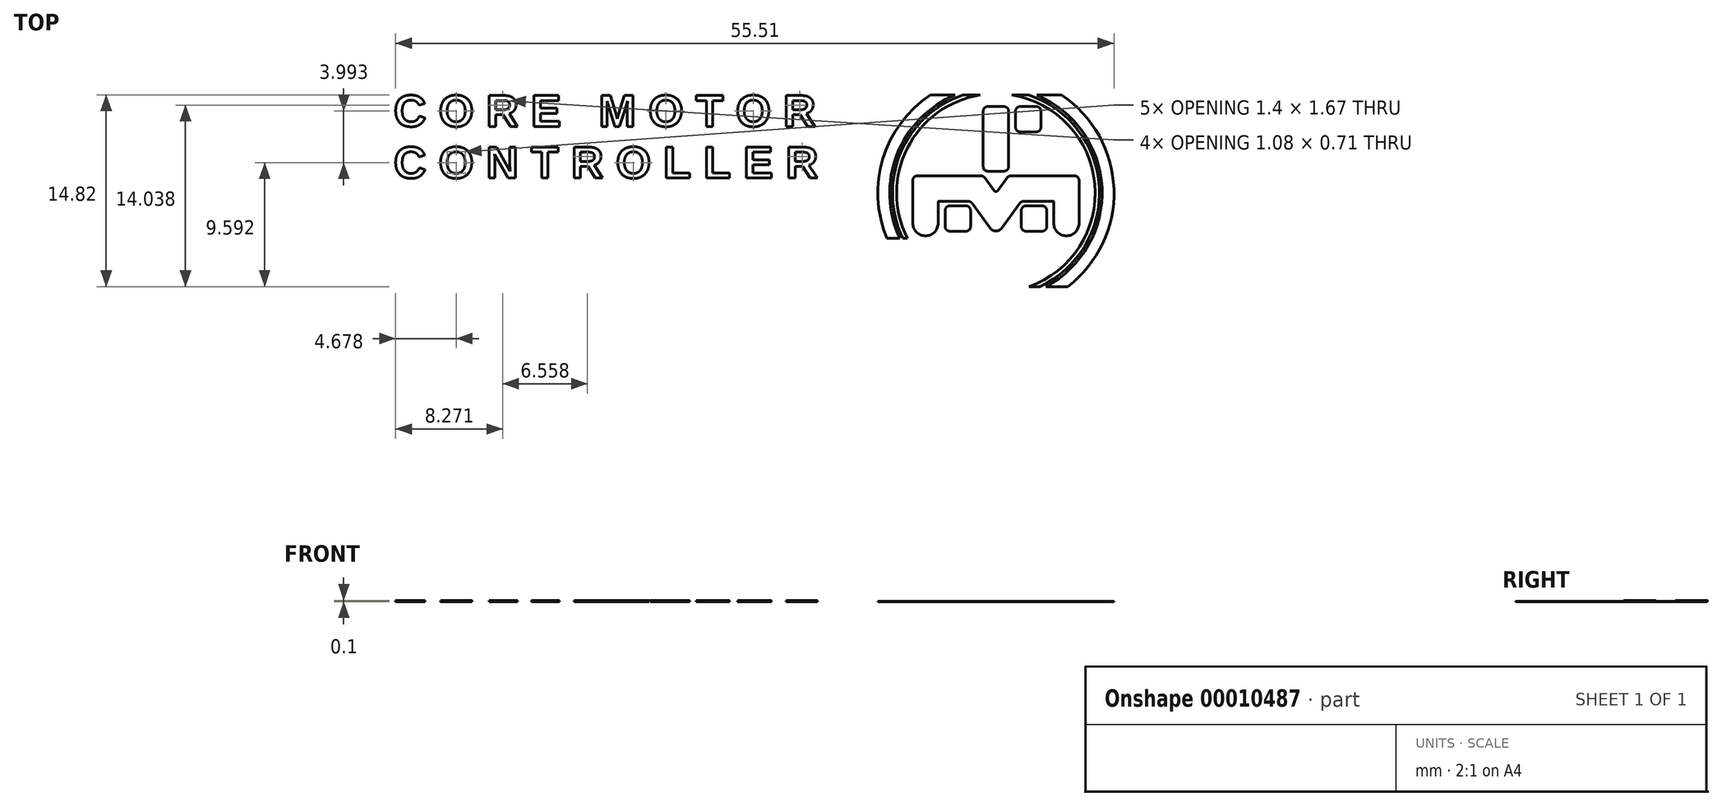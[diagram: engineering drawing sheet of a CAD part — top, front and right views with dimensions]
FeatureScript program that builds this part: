
annotation { "Feature Type Name" : "Feature", "Feature Type Description" : "" }
export const myFeature = defineFeature(function(context is Context, id is Id, definition is map)
    precondition{}
    {
        {
            var Q0;
            Q0=qCreatedBy(makeId("Top.planeOp"),FACE);
            var sketch = newSketch(context, id + "F0", { "sketchPlane" : qUnion([Q0])});
            skLineSegment(sketch, "E0.bottom", {"start": v(62.75, -5.5) * mm, "end": v(66.25, -5.5) * mm});
            skLineSegment(sketch, "E0.top", {"start": v(62.75, -19.5) * mm, "end": v(66.25, -19.5) * mm});
            skLineSegment(sketch, "E0.left", {"start": v(61.75, -6.5) * mm, "end": v(61.75, -18.5) * mm});
            skLineSegment(sketch, "E0.right", {"start": v(67.25, -6.5) * mm, "end": v(67.25, -18.5) * mm});
            skLineSegment(sketch, "E1.bottom", {"start": v(69.75, -5.5) * mm, "end": v(73.25, -5.5) * mm});
            skLineSegment(sketch, "E1.top", {"start": v(69.75, -11) * mm, "end": v(73.25, -11) * mm});
            skLineSegment(sketch, "E1.left", {"start": v(68.75, -6.5) * mm, "end": v(68.75, -10) * mm});
            skLineSegment(sketch, "E1.right", {"start": v(74.25, -6.5) * mm, "end": v(74.25, -10) * mm});
            skLineSegment(sketch, "E2", {"start": v(64.5, -19.5) * mm, "end": v(64.5, -33.5) * mm, "construction": true});
            skLineSegment(sketch, "E3", {"start": v(63.3, -31.86) * mm, "end": v(59.27, -26.4) * mm});
            skLineSegment(sketch, "E4", {"start": v(58.47, -26) * mm, "end": v(52.1, -26) * mm});
            skLineSegment(sketch, "E5", {"start": v(52, -26.1) * mm, "end": v(52, -30.75) * mm});
            skLineSegment(sketch, "E6.0", {"start": v(46.5, -21.5) * mm, "end": v(46.5, -30.75) * mm});
            skLineSegment(sketch, "E6.1", {"start": v(61.24, -20.5) * mm, "end": v(47.5, -20.5) * mm});
            skLineSegment(sketch, "E6.2", {"start": v(64.1, -23.68) * mm, "end": v(62.05, -20.9) * mm});
            skLineSegment(sketch, "E7", {"start": v(49.25, -33.5) * mm, "end": v(49.25, -33.5) * mm});
            skPoint(sketch, "E8.orphan", {"position": v(52, -33.5) * mm});
            skPoint(sketch, "E9.visualSharp", {"position": v(46.5, -33.5) * mm});
            skArc(sketch, "E9.filletArc", {"start": v(46.5, -30.75) * mm, "mid": v(47.3, -32.7) * mm, "end": v(49.25, -33.5) * mm});
            skArc(sketch, "E10.filletArc", {"start": v(49.25, -33.5) * mm, "mid": v(51.2, -32.7) * mm, "end": v(52, -30.75) * mm});
            skLineSegment(sketch, "E11.right", {"start": v(59, -28) * mm, "end": v(59, -31.5) * mm});
            skLineSegment(sketch, "E11.left", {"start": v(53.5, -28) * mm, "end": v(53.5, -31.5) * mm});
            skLineSegment(sketch, "E11.top", {"start": v(54.5, -32.5) * mm, "end": v(58, -32.5) * mm});
            skLineSegment(sketch, "E11.bottom", {"start": v(54.5, -27) * mm, "end": v(58, -27) * mm});
            skPoint(sketch, "E12.0.MirrorP", {"position": v(77, -33.5) * mm});
            skLineSegment(sketch, "E12.1.MirrorCS", {"start": v(74.5, -27) * mm, "end": v(71, -27) * mm});
            skPoint(sketch, "E12.2.MirrorP", {"position": v(82.5, -33.5) * mm});
            skLineSegment(sketch, "E12.3.MirrorCS", {"start": v(70, -28) * mm, "end": v(70, -31.5) * mm});
            skLineSegment(sketch, "E12.4.MirrorCS", {"start": v(75.5, -28) * mm, "end": v(75.5, -31.5) * mm});
            skLineSegment(sketch, "E12.5.MirrorCS", {"start": v(74.5, -32.5) * mm, "end": v(71, -32.5) * mm});
            skLineSegment(sketch, "E12.6.MirrorCS", {"start": v(70.53, -26) * mm, "end": v(76.9, -26) * mm});
            skLineSegment(sketch, "E12.7.MirrorCS", {"start": v(77, -26.1) * mm, "end": v(77, -30.75) * mm});
            skArc(sketch, "E12.8.MirrorCS", {"start": v(79.75, -33.5) * mm, "mid": v(77.8, -32.7) * mm, "end": v(77, -30.75) * mm});
            skLineSegment(sketch, "E12.9.MirrorCS", {"start": v(79.75, -33.5) * mm, "end": v(79.75, -33.5) * mm});
            skLineSegment(sketch, "E12.10.MirrorCS", {"start": v(67.76, -20.5) * mm, "end": v(81.5, -20.5) * mm});
            skPoint(sketch, "E12.11.MirrorP", {"position": v(77, -33.5) * mm});
            skLineSegment(sketch, "E12.12.MirrorCS", {"start": v(64.9, -23.68) * mm, "end": v(66.95, -20.9) * mm});
            skArc(sketch, "E12.13.MirrorCS", {"start": v(82.5, -30.75) * mm, "mid": v(81.7, -32.7) * mm, "end": v(79.75, -33.5) * mm});
            skLineSegment(sketch, "E12.14.MirrorCS", {"start": v(65.7, -31.86) * mm, "end": v(69.73, -26.4) * mm});
            skLineSegment(sketch, "E12.15.MirrorCS", {"start": v(82.5, -21.5) * mm, "end": v(82.5, -30.75) * mm});
            skPoint(sketch, "E13.visualSharp", {"position": v(68.75, -5.5) * mm});
            skArc(sketch, "E13.filletArc", {"start": v(69.75, -5.5) * mm, "mid": v(69.04, -5.8) * mm, "end": v(68.75, -6.5) * mm});
            skPoint(sketch, "E14.visualSharp", {"position": v(74.25, -5.5) * mm});
            skArc(sketch, "E14.filletArc", {"start": v(74.25, -6.5) * mm, "mid": v(73.96, -5.8) * mm, "end": v(73.25, -5.5) * mm});
            skPoint(sketch, "E15.visualSharp", {"position": v(74.25, -11) * mm});
            skArc(sketch, "E15.filletArc", {"start": v(73.25, -11) * mm, "mid": v(73.96, -10.7) * mm, "end": v(74.25, -10) * mm});
            skPoint(sketch, "E16.visualSharp", {"position": v(68.75, -11) * mm});
            skArc(sketch, "E16.filletArc", {"start": v(68.75, -10) * mm, "mid": v(69.04, -10.7) * mm, "end": v(69.75, -11) * mm});
            skPoint(sketch, "E17.visualSharp", {"position": v(67.25, -5.5) * mm});
            skArc(sketch, "E17.filletArc", {"start": v(67.25, -6.5) * mm, "mid": v(66.96, -5.8) * mm, "end": v(66.25, -5.5) * mm});
            skPoint(sketch, "E18.visualSharp", {"position": v(61.75, -5.5) * mm});
            skArc(sketch, "E18.filletArc", {"start": v(62.75, -5.5) * mm, "mid": v(62.04, -5.8) * mm, "end": v(61.75, -6.5) * mm});
            skPoint(sketch, "E19.visualSharp", {"position": v(61.75, -19.5) * mm});
            skArc(sketch, "E19.filletArc", {"start": v(61.75, -18.5) * mm, "mid": v(62.04, -19.2) * mm, "end": v(62.75, -19.5) * mm});
            skPoint(sketch, "E20.visualSharp", {"position": v(67.25, -19.5) * mm});
            skArc(sketch, "E20.filletArc", {"start": v(66.25, -19.5) * mm, "mid": v(66.96, -19.2) * mm, "end": v(67.25, -18.5) * mm});
            skPoint(sketch, "E21.visualSharp", {"position": v(70, -32.5) * mm});
            skArc(sketch, "E21.filletArc", {"start": v(70, -31.5) * mm, "mid": v(70.3, -32.2) * mm, "end": v(71, -32.5) * mm});
            skPoint(sketch, "E22.visualSharp", {"position": v(75.5, -27) * mm});
            skArc(sketch, "E22.filletArc", {"start": v(75.5, -28) * mm, "mid": v(75.2, -27.3) * mm, "end": v(74.5, -27) * mm});
            skPoint(sketch, "E23.visualSharp", {"position": v(70, -27) * mm});
            skArc(sketch, "E23.filletArc", {"start": v(71, -27) * mm, "mid": v(70.3, -27.3) * mm, "end": v(70, -28) * mm});
            skPoint(sketch, "E24.visualSharp", {"position": v(75.5, -32.5) * mm});
            skArc(sketch, "E24.filletArc", {"start": v(74.5, -32.5) * mm, "mid": v(75.2, -32.2) * mm, "end": v(75.5, -31.5) * mm});
            skPoint(sketch, "E25.visualSharp", {"position": v(59, -32.5) * mm});
            skArc(sketch, "E25.filletArc", {"start": v(58, -32.5) * mm, "mid": v(58.7, -32.2) * mm, "end": v(59, -31.5) * mm});
            skPoint(sketch, "E26.visualSharp", {"position": v(59, -27) * mm});
            skArc(sketch, "E26.filletArc", {"start": v(59, -28) * mm, "mid": v(58.7, -27.3) * mm, "end": v(58, -27) * mm});
            skPoint(sketch, "E27.visualSharp", {"position": v(53.5, -27) * mm});
            skArc(sketch, "E27.filletArc", {"start": v(54.5, -27) * mm, "mid": v(53.8, -27.3) * mm, "end": v(53.5, -28) * mm});
            skPoint(sketch, "E28.visualSharp", {"position": v(53.5, -32.5) * mm});
            skArc(sketch, "E28.filletArc", {"start": v(53.5, -31.5) * mm, "mid": v(53.8, -32.2) * mm, "end": v(54.5, -32.5) * mm});
            skPoint(sketch, "E29.visualSharp", {"position": v(46.5, -20.5) * mm});
            skArc(sketch, "E29.filletArc", {"start": v(47.5, -20.5) * mm, "mid": v(46.8, -20.8) * mm, "end": v(46.5, -21.5) * mm});
            skPoint(sketch, "E30.visualSharp", {"position": v(82.5, -20.5) * mm});
            skArc(sketch, "E30.filletArc", {"start": v(82.5, -21.5) * mm, "mid": v(82.2, -20.8) * mm, "end": v(81.5, -20.5) * mm});
            skPoint(sketch, "E31.visualSharp", {"position": v(61.75, -20.5) * mm});
            skArc(sketch, "E31.filletArc", {"start": v(62.05, -20.9) * mm, "mid": v(61.7, -20.6) * mm, "end": v(61.24, -20.5) * mm});
            skPoint(sketch, "E32.visualSharp", {"position": v(67.25, -20.5) * mm});
            skArc(sketch, "E32.filletArc", {"start": v(67.76, -20.5) * mm, "mid": v(67.3, -20.6) * mm, "end": v(66.95, -20.9) * mm});
            skPoint(sketch, "E33.visualSharp", {"position": v(52, -26) * mm});
            skArc(sketch, "E33.filletArc", {"start": v(52.1, -26) * mm, "mid": v(52.03, -26.03) * mm, "end": v(52, -26.1) * mm});
            skPoint(sketch, "E34.visualSharp", {"position": v(77, -26) * mm});
            skArc(sketch, "E34.filletArc", {"start": v(77, -26.1) * mm, "mid": v(76.97, -26.03) * mm, "end": v(76.9, -26) * mm});
            skPoint(sketch, "E35.visualSharp", {"position": v(70.03, -26) * mm});
            skArc(sketch, "E35.filletArc", {"start": v(70.53, -26) * mm, "mid": v(70.08, -26.1) * mm, "end": v(69.73, -26.4) * mm});
            skPoint(sketch, "E36.visualSharp", {"position": v(58.97, -26) * mm});
            skArc(sketch, "E36.filletArc", {"start": v(59.27, -26.4) * mm, "mid": v(58.92, -26.1) * mm, "end": v(58.47, -26) * mm});
            skPoint(sketch, "E37.visualSharp", {"position": v(64.5, -33.5) * mm});
            skArc(sketch, "E37.filletArc", {"start": v(63.3, -31.86) * mm, "mid": v(64.5, -32.47) * mm, "end": v(65.7, -31.86) * mm});
            skPoint(sketch, "E38.visualSharp", {"position": v(64.5, -24.23) * mm});
            skArc(sketch, "E38.filletArc", {"start": v(64.1, -23.68) * mm, "mid": v(64.5, -23.89) * mm, "end": v(64.9, -23.68) * mm});
            skArc(sketch, "E39", {"start": v(71.68, -44.5) * mm, "mid": v(85.92, -22.29) * mm, "end": v(67.92, -3) * mm});
            skArc(sketch, "E40", {"start": v(74, -44.5) * mm, "mid": v(86.85, -22.94) * mm, "end": v(71.6, -3) * mm});
            skArc(sketch, "E41", {"start": v(75.35, -44.5) * mm, "mid": v(87.46, -23.1) * mm, "end": v(73.32, -3) * mm});
            skArc(sketch, "E42", {"start": v(80.06, -44.5) * mm, "mid": v(90.04, -23.4) * mm, "end": v(78.72, -3) * mm});
            skLineSegment(sketch, "E43", {"start": v(80.06, -44.5) * mm, "end": v(75.35, -44.5) * mm});
            skLineSegment(sketch, "E44.trimOffspring", {"start": v(74, -44.5) * mm, "end": v(71.68, -44.5) * mm});
            skLineSegment(sketch, "E45", {"start": v(40.9, -34) * mm, "end": v(43.69, -34) * mm});
            skLineSegment(sketch, "E46.trimOffspring", {"start": v(44.36, -34) * mm, "end": v(45.34, -34) * mm});
            skLineSegment(sketch, "E47", {"start": v(50.28, -3) * mm, "end": v(55.68, -3) * mm});
            skArc(sketch, "E48.trimOffspring", {"start": v(61.08, -3) * mm, "mid": v(45.33, -14.5) * mm, "end": v(45.34, -34) * mm});
            skArc(sketch, "E49.trimOffspring", {"start": v(50.28, -3) * mm, "mid": v(40.05, -16.82) * mm, "end": v(40.9, -34) * mm});
            skArc(sketch, "E50.trimOffspring", {"start": v(55.68, -3) * mm, "mid": v(43.06, -15.94) * mm, "end": v(43.69, -34) * mm});
            skArc(sketch, "E51.trimOffspring", {"start": v(57.4, -3) * mm, "mid": v(43.86, -15.55) * mm, "end": v(44.36, -34) * mm});
            skLineSegment(sketch, "E52.trimOffspring", {"start": v(67.92, -3) * mm, "end": v(71.6, -3) * mm});
            skLineSegment(sketch, "E53.trimOffspring", {"start": v(57.4, -3) * mm, "end": v(61.08, -3) * mm});
            skLineSegment(sketch, "E54.trimOffspring", {"start": v(73.32, -3) * mm, "end": v(78.72, -3) * mm});
            skSolve(sketch);
        }
        {
            var Q0;
            Q0=makeQuery(id+"F0.imprint","IMPRINT",FACE,{"disambiguationData":[TD([[makeQuery(id+"F0.imprint","IMPRINT",EDGE,{"derivedFrom":sQuery(id+"F0.wireOp",EDGE,"46c11c21-c6ca-42b8-9659-15b4f280ee3c.sketch_text.stroke-197")}),1.0]])]});
            var Q1;
            Q1=makeQuery(id+"F0.imprint","IMPRINT",FACE,{"disambiguationData":[TD([[makeQuery(id+"F0.imprint","IMPRINT",EDGE,{"derivedFrom":sQuery(id+"F0.wireOp",EDGE,"E1.bottom")}),-1.0]])]});
            var Q2;
            Q2=makeQuery(id+"F0.imprint","IMPRINT",FACE,{"disambiguationData":[TD([[makeQuery(id+"F0.imprint","IMPRINT",EDGE,{"derivedFrom":sQuery(id+"F0.wireOp",EDGE,"46c11c21-c6ca-42b8-9659-15b4f280ee3c.sketch_text.stroke-126")}),-1.0]])]});
            var Q3;
            Q3=makeQuery(id+"F0.imprint","IMPRINT",FACE,{"disambiguationData":[TD([[makeQuery(id+"F0.imprint","IMPRINT",EDGE,{"derivedFrom":sQuery(id+"F0.wireOp",EDGE,"46c11c21-c6ca-42b8-9659-15b4f280ee3c.sketch_text.stroke-360")}),-1.0]])]});
            var Q4;
            Q4=makeQuery(id+"F0.imprint","IMPRINT",FACE,{"disambiguationData":[TD([[makeQuery(id+"F0.imprint","IMPRINT",EDGE,{"derivedFrom":sQuery(id+"F0.wireOp",EDGE,"E0.bottom")}),-1.0]])]});
            var Q5;
            Q5=makeQuery(id+"F0.imprint","IMPRINT",FACE,{"disambiguationData":[TD([[makeQuery(id+"F0.imprint","IMPRINT",EDGE,{"derivedFrom":sQuery(id+"F0.wireOp",EDGE,"46c11c21-c6ca-42b8-9659-15b4f280ee3c.sketch_text.stroke-0")}),-1.0]])]});
            var Q6;
            Q6=makeQuery(id+"F0.imprint","IMPRINT",FACE,{"disambiguationData":[TD([[makeQuery(id+"F0.imprint","IMPRINT",EDGE,{"derivedFrom":sQuery(id+"F0.wireOp",EDGE,"46c11c21-c6ca-42b8-9659-15b4f280ee3c.sketch_text.stroke-90")}),-1.0]])]});
            var Q7;
            Q7=makeQuery(id+"F0.imprint","IMPRINT",FACE,{"disambiguationData":[TD([[makeQuery(id+"F0.imprint","IMPRINT",EDGE,{"derivedFrom":sQuery(id+"F0.wireOp",EDGE,"46c11c21-c6ca-42b8-9659-15b4f280ee3c.sketch_text.stroke-145")}),-1.0]])]});
            var Q8;
            Q8=makeQuery(id+"F0.imprint","IMPRINT",FACE,{"disambiguationData":[TD([[makeQuery(id+"F0.imprint","IMPRINT",EDGE,{"derivedFrom":sQuery(id+"F0.wireOp",EDGE,"46c11c21-c6ca-42b8-9659-15b4f280ee3c.sketch_text.stroke-126")}),1.0]])]});
            var Q9;
            Q9=makeQuery(id+"F0.imprint","IMPRINT",FACE,{"disambiguationData":[TD([[makeQuery(id+"F0.imprint","IMPRINT",EDGE,{"derivedFrom":sQuery(id+"F0.wireOp",EDGE,"46c11c21-c6ca-42b8-9659-15b4f280ee3c.sketch_text.stroke-48")}),-1.0]])]});
            var Q10;
            Q10=makeQuery(id+"F0.imprint","IMPRINT",FACE,{"disambiguationData":[TD([[makeQuery(id+"F0.imprint","IMPRINT",EDGE,{"derivedFrom":sQuery(id+"F0.wireOp",EDGE,"46c11c21-c6ca-42b8-9659-15b4f280ee3c.sketch_text.stroke-239")}),1.0]])]});
            var Q11;
            Q11=makeQuery(id+"F0.imprint","IMPRINT",FACE,{"disambiguationData":[TD([[makeQuery(id+"F0.imprint","IMPRINT",EDGE,{"derivedFrom":sQuery(id+"F0.wireOp",EDGE,"E12.1.MirrorCS")}),1.0]])]});
            var Q12;
            Q12=makeQuery(id+"F0.imprint","IMPRINT",FACE,{"disambiguationData":[TD([[makeQuery(id+"F0.imprint","IMPRINT",EDGE,{"derivedFrom":sQuery(id+"F0.wireOp",EDGE,"46c11c21-c6ca-42b8-9659-15b4f280ee3c.sketch_text.stroke-300")}),-1.0]])]});
            var Q13;
            Q13=makeQuery(id+"F0.imprint","IMPRINT",FACE,{"disambiguationData":[TD([[makeQuery(id+"F0.imprint","IMPRINT",EDGE,{"derivedFrom":sQuery(id+"F0.wireOp",EDGE,"46c11c21-c6ca-42b8-9659-15b4f280ee3c.sketch_text.stroke-245")}),-1.0]])]});
            var Q14;
            Q14=makeQuery(id+"F0.imprint","IMPRINT",FACE,{"disambiguationData":[TD([[makeQuery(id+"F0.imprint","IMPRINT",EDGE,{"derivedFrom":sQuery(id+"F0.wireOp",EDGE,"46c11c21-c6ca-42b8-9659-15b4f280ee3c.sketch_text.stroke-268")}),-1.0]])]});
            var Q15;
            Q15=makeQuery(id+"F0.imprint","IMPRINT",FACE,{"disambiguationData":[TD([[makeQuery(id+"F0.imprint","IMPRINT",EDGE,{"derivedFrom":sQuery(id+"F0.wireOp",EDGE,"46c11c21-c6ca-42b8-9659-15b4f280ee3c.sketch_text.stroke-189")}),-1.0]])]});
            var Q16;
            Q16=makeQuery(id+"F0.imprint","IMPRINT",FACE,{"disambiguationData":[TD([[makeQuery(id+"F0.imprint","IMPRINT",EDGE,{"derivedFrom":sQuery(id+"F0.wireOp",EDGE,"46c11c21-c6ca-42b8-9659-15b4f280ee3c.sketch_text.stroke-114")}),-1.0]])]});
            var Q17;
            Q17=makeQuery(id+"F0.imprint","IMPRINT",FACE,{"disambiguationData":[TD([[makeQuery(id+"F0.imprint","IMPRINT",EDGE,{"derivedFrom":sQuery(id+"F0.wireOp",EDGE,"E3")}),-1.0]])]});
            var Q18;
            Q18=makeQuery(id+"F0.imprint","IMPRINT",FACE,{"disambiguationData":[TD([[makeQuery(id+"F0.imprint","IMPRINT",EDGE,{"derivedFrom":sQuery(id+"F0.wireOp",EDGE,"46c11c21-c6ca-42b8-9659-15b4f280ee3c.sketch_text.stroke-345")}),-1.0]])]});
            var Q19;
            Q19=makeQuery(id+"F0.imprint","IMPRINT",FACE,{"disambiguationData":[TD([[makeQuery(id+"F0.imprint","IMPRINT",EDGE,{"derivedFrom":sQuery(id+"F0.wireOp",EDGE,"46c11c21-c6ca-42b8-9659-15b4f280ee3c.sketch_text.stroke-232")}),1.0]])]});
            var Q20;
            Q20=makeQuery(id+"F0.imprint","IMPRINT",FACE,{"disambiguationData":[TD([[makeQuery(id+"F0.imprint","IMPRINT",EDGE,{"derivedFrom":sQuery(id+"F0.wireOp",EDGE,"46c11c21-c6ca-42b8-9659-15b4f280ee3c.sketch_text.stroke-280")}),1.0]])]});
            var Q21;
            Q21=makeQuery(id+"F0.imprint","IMPRINT",FACE,{"disambiguationData":[TD([[makeQuery(id+"F0.imprint","IMPRINT",EDGE,{"derivedFrom":sQuery(id+"F0.wireOp",EDGE,"46c11c21-c6ca-42b8-9659-15b4f280ee3c.sketch_text.stroke-161")}),-1.0]])]});
            var Q22;
            Q22=makeQuery(id+"F0.imprint","IMPRINT",FACE,{"disambiguationData":[TD([[makeQuery(id+"F0.imprint","IMPRINT",EDGE,{"derivedFrom":sQuery(id+"F0.wireOp",EDGE,"46c11c21-c6ca-42b8-9659-15b4f280ee3c.sketch_text.stroke-157")}),-1.0]])]});
            var Q23;
            Q23=makeQuery(id+"F0.imprint","IMPRINT",FACE,{"disambiguationData":[TD([[makeQuery(id+"F0.imprint","IMPRINT",EDGE,{"derivedFrom":sQuery(id+"F0.wireOp",EDGE,"46c11c21-c6ca-42b8-9659-15b4f280ee3c.sketch_text.stroke-84")}),1.0]])]});
            var Q24;
            Q24=makeQuery(id+"F0.imprint","IMPRINT",FACE,{"disambiguationData":[TD([[makeQuery(id+"F0.imprint","IMPRINT",EDGE,{"derivedFrom":sQuery(id+"F0.wireOp",EDGE,"46c11c21-c6ca-42b8-9659-15b4f280ee3c.sketch_text.stroke-60")}),-1.0]])]});
            var Q25;
            Q25=makeQuery(id+"F0.imprint","IMPRINT",FACE,{"disambiguationData":[TD([[makeQuery(id+"F0.imprint","IMPRINT",EDGE,{"derivedFrom":sQuery(id+"F0.wireOp",EDGE,"46c11c21-c6ca-42b8-9659-15b4f280ee3c.sketch_text.stroke-340")}),1.0]])]});
            var Q26;
            Q26=makeQuery(id+"F0.imprint","IMPRINT",FACE,{"disambiguationData":[TD([[makeQuery(id+"F0.imprint","IMPRINT",EDGE,{"derivedFrom":sQuery(id+"F0.wireOp",EDGE,"46c11c21-c6ca-42b8-9659-15b4f280ee3c.sketch_text.stroke-220")}),-1.0]])]});
            var Q27;
            Q27=makeQuery(id+"F0.imprint","IMPRINT",FACE,{"disambiguationData":[TD([[makeQuery(id+"F0.imprint","IMPRINT",EDGE,{"derivedFrom":sQuery(id+"F0.wireOp",EDGE,"46c11c21-c6ca-42b8-9659-15b4f280ee3c.sketch_text.stroke-76")}),-1.0]])]});
            var Q28;
            Q28=makeQuery(id+"F0.imprint","IMPRINT",FACE,{"disambiguationData":[TD([[makeQuery(id+"F0.imprint","IMPRINT",EDGE,{"derivedFrom":sQuery(id+"F0.wireOp",EDGE,"46c11c21-c6ca-42b8-9659-15b4f280ee3c.sketch_text.stroke-327")}),1.0]])]});
            var Q29;
            Q29=makeQuery(id+"F0.imprint","IMPRINT",FACE,{"disambiguationData":[TD([[makeQuery(id+"F0.imprint","IMPRINT",EDGE,{"derivedFrom":sQuery(id+"F0.wireOp",EDGE,"46c11c21-c6ca-42b8-9659-15b4f280ee3c.sketch_text.stroke-29")}),-1.0]])]});
            var Q30;
            Q30=makeQuery(id+"F0.imprint","IMPRINT",FACE,{"disambiguationData":[TD([[makeQuery(id+"F0.imprint","IMPRINT",EDGE,{"derivedFrom":sQuery(id+"F0.wireOp",EDGE,"46c11c21-c6ca-42b8-9659-15b4f280ee3c.sketch_text.stroke-60")}),1.0]])]});
            var Q31;
            Q31=makeQuery(id+"F0.imprint","IMPRINT",FACE,{"disambiguationData":[TD([[makeQuery(id+"F0.imprint","IMPRINT",EDGE,{"derivedFrom":sQuery(id+"F0.wireOp",EDGE,"46c11c21-c6ca-42b8-9659-15b4f280ee3c.sketch_text.stroke-333")}),-1.0]])]});
            var Q32;
            Q32=makeQuery(id+"F0.imprint","IMPRINT",FACE,{"disambiguationData":[TD([[makeQuery(id+"F0.imprint","IMPRINT",EDGE,{"derivedFrom":sQuery(id+"F0.wireOp",EDGE,"E11.right")}),-1.0]])]});
            var Q33;
            Q33=makeQuery(id+"F0.imprint","IMPRINT",FACE,{"disambiguationData":[TD([[makeQuery(id+"F0.imprint","IMPRINT",EDGE,{"derivedFrom":sQuery(id+"F0.wireOp",EDGE,"46c11c21-c6ca-42b8-9659-15b4f280ee3c.sketch_text.stroke-216")}),-1.0]])]});
            var Q34;
            Q34=makeQuery(id+"F0.imprint","IMPRINT",FACE,{"disambiguationData":[TD([[makeQuery(id+"F0.imprint","IMPRINT",EDGE,{"derivedFrom":sQuery(id+"F0.wireOp",EDGE,"46c11c21-c6ca-42b8-9659-15b4f280ee3c.sketch_text.stroke-260")}),-1.0]])]});
            var Q35;
            Q35=makeQuery(id+"F0.imprint","IMPRINT",FACE,{"disambiguationData":[TD([[makeQuery(id+"F0.imprint","IMPRINT",EDGE,{"derivedFrom":sQuery(id+"F0.wireOp",EDGE,"46c11c21-c6ca-42b8-9659-15b4f280ee3c.sketch_text.stroke-286")}),-1.0]])]});
            var Q36;
            Q36=makeQuery(id+"F0.imprint","IMPRINT",FACE,{"disambiguationData":[TD([[makeQuery(id+"F0.imprint","IMPRINT",EDGE,{"derivedFrom":sQuery(id+"F0.wireOp",EDGE,"46c11c21-c6ca-42b8-9659-15b4f280ee3c.sketch_text.stroke-197")}),-1.0]])]});
            var Q37;
            Q37=makeQuery(id+"F0.imprint","IMPRINT",FACE,{"disambiguationData":[TD([[makeQuery(id+"F0.imprint","IMPRINT",EDGE,{"derivedFrom":sQuery(id+"F0.wireOp",EDGE,"46c11c21-c6ca-42b8-9659-15b4f280ee3c.sketch_text.stroke-319")}),-1.0]])]});
            var Q38;
            Q38=makeQuery(id+"F0.imprint","IMPRINT",FACE,{"disambiguationData":[TD([[makeQuery(id+"F0.imprint","IMPRINT",EDGE,{"derivedFrom":sQuery(id+"F0.wireOp",EDGE,"46c11c21-c6ca-42b8-9659-15b4f280ee3c.sketch_text.stroke-366")}),-1.0]])]});
            var Q39;
            Q39=makeQuery(id+"F0.imprint","IMPRINT",FACE,{"disambiguationData":[TD([[makeQuery(id+"F0.imprint","IMPRINT",EDGE,{"derivedFrom":sQuery(id+"F0.wireOp",EDGE,"46c11c21-c6ca-42b8-9659-15b4f280ee3c.sketch_text.stroke-272")}),-1.0]])]});
            var Q40;
            Q40=makeQuery(id+"F0.imprint","IMPRINT",FACE,{"disambiguationData":[TD([[makeQuery(id+"F0.imprint","IMPRINT",EDGE,{"derivedFrom":sQuery(id+"F0.wireOp",EDGE,"46c11c21-c6ca-42b8-9659-15b4f280ee3c.sketch_text.stroke-15")}),-1.0]])]});
            var Q41;
            Q41=makeQuery(id+"F0.imprint","IMPRINT",FACE,{"disambiguationData":[TD([[makeQuery(id+"F0.imprint","IMPRINT",EDGE,{"derivedFrom":sQuery(id+"F0.wireOp",EDGE,"46c11c21-c6ca-42b8-9659-15b4f280ee3c.sketch_text.stroke-168")}),-1.0]])]});
            var Q42;
            Q42=makeQuery(id+"F0.imprint","IMPRINT",FACE,{"disambiguationData":[TD([[makeQuery(id+"F0.imprint","IMPRINT",EDGE,{"derivedFrom":sQuery(id+"F0.wireOp",EDGE,"46c11c21-c6ca-42b8-9659-15b4f280ee3c.sketch_text.stroke-95")}),-1.0]])]});
            var Q43;
            Q43=makeQuery(id+"F0.imprint","IMPRINT",FACE,{"disambiguationData":[TD([[makeQuery(id+"F0.imprint","IMPRINT",EDGE,{"derivedFrom":sQuery(id+"F0.wireOp",EDGE,"46c11c21-c6ca-42b8-9659-15b4f280ee3c.sketch_text.stroke-225")}),-1.0]])]});
            var Q44;
            Q44=makeQuery(id+"F0.imprint","IMPRINT",FACE,{"disambiguationData":[TD([[makeQuery(id+"F0.imprint","IMPRINT",EDGE,{"derivedFrom":sQuery(id+"F0.wireOp",EDGE,"46c11c21-c6ca-42b8-9659-15b4f280ee3c.sketch_text.stroke-231")}),-1.0]])]});
            var Q45;
            Q45=makeQuery(id+"F0.imprint","IMPRINT",FACE,{"disambiguationData":[TD([[makeQuery(id+"F0.imprint","IMPRINT",EDGE,{"derivedFrom":sQuery(id+"F0.wireOp",EDGE,"46c11c21-c6ca-42b8-9659-15b4f280ee3c.sketch_text.stroke-177")}),-1.0]])]});
            var Q46;
            Q46=makeQuery(id+"F0.imprint","IMPRINT",FACE,{"disambiguationData":[TD([[makeQuery(id+"F0.imprint","IMPRINT",EDGE,{"derivedFrom":sQuery(id+"F0.wireOp",EDGE,"E41")}),-1.0]])]});
            var Q47;
            Q47=makeQuery(id+"F0.imprint","IMPRINT",FACE,{"disambiguationData":[TD([[makeQuery(id+"F0.imprint","IMPRINT",EDGE,{"derivedFrom":sQuery(id+"F0.wireOp",EDGE,"E39")}),-1.0]])]});
            var Q48;
            Q48=makeQuery(id+"F0.imprint","IMPRINT",FACE,{"disambiguationData":[TD([[makeQuery(id+"F0.imprint","IMPRINT",EDGE,{"derivedFrom":sQuery(id+"F0.wireOp",EDGE,"E45")}),1.0]])]});
            var Q49;
            Q49=makeQuery(id+"F0.imprint","IMPRINT",FACE,{"disambiguationData":[TD([[makeQuery(id+"F0.imprint","IMPRINT",EDGE,{"derivedFrom":sQuery(id+"F0.wireOp",EDGE,"E46.trimOffspring")}),1.0]])]});
            extrude(context, id + "F1", {"entities" : qUnion([Q0, Q1, Q2, Q3, Q4, Q5, Q6, Q7, Q8, Q9, Q10, Q11, Q12, Q13, Q14, Q15, Q16, Q17, Q18, Q19, Q20, Q21, Q22, Q23, Q24, Q25, Q26, Q27, Q28, Q29, Q30, Q31, Q32, Q33, Q34, Q35, Q36, Q37, Q38, Q39, Q40, Q41, Q42, Q43, Q44, Q45, Q46, Q47, Q48, Q49]), "depth" : .1 * mm});
        }
        {
            var Q0;
            Q0=makeQuery(id+"F1.opExtrude","SWEPT_BODY",BODY,{"disambiguationData":[OSD([sQuery(id+"F0.wireOp",EDGE,"46c11c21-c6ca-42b8-9659-15b4f280ee3c.sketch_text.stroke-149"),sQuery(id+"F0.wireOp",EDGE,"46c11c21-c6ca-42b8-9659-15b4f280ee3c.sketch_text.stroke-150"),sQuery(id+"F0.wireOp",EDGE,"46c11c21-c6ca-42b8-9659-15b4f280ee3c.sketch_text.stroke-151"),sQuery(id+"F0.wireOp",EDGE,"46c11c21-c6ca-42b8-9659-15b4f280ee3c.sketch_text.stroke-152"),sQuery(id+"F0.wireOp",EDGE,"46c11c21-c6ca-42b8-9659-15b4f280ee3c.sketch_text.stroke-153"),sQuery(id+"F0.wireOp",EDGE,"46c11c21-c6ca-42b8-9659-15b4f280ee3c.sketch_text.stroke-154"),sQuery(id+"F0.wireOp",EDGE,"46c11c21-c6ca-42b8-9659-15b4f280ee3c.sketch_text.stroke-155"),sQuery(id+"F0.wireOp",EDGE,"46c11c21-c6ca-42b8-9659-15b4f280ee3c.sketch_text.stroke-156"),sQuery(id+"F0.wireOp",EDGE,"46c11c21-c6ca-42b8-9659-15b4f280ee3c.sketch_text.stroke-157"),sQuery(id+"F0.wireOp",EDGE,"46c11c21-c6ca-42b8-9659-15b4f280ee3c.sketch_text.stroke-158"),sQuery(id+"F0.wireOp",EDGE,"46c11c21-c6ca-42b8-9659-15b4f280ee3c.sketch_text.stroke-159"),sQuery(id+"F0.wireOp",EDGE,"46c11c21-c6ca-42b8-9659-15b4f280ee3c.sketch_text.stroke-160"),sQuery(id+"F0.wireOp",EDGE,"46c11c21-c6ca-42b8-9659-15b4f280ee3c.sketch_text.stroke-161"),sQuery(id+"F0.wireOp",EDGE,"46c11c21-c6ca-42b8-9659-15b4f280ee3c.sketch_text.stroke-162")])]});
            var Q1;
            Q1=makeQuery(id+"F1.opExtrude","SWEPT_BODY",BODY,{"disambiguationData":[OSD([sQuery(id+"F0.wireOp",EDGE,"46c11c21-c6ca-42b8-9659-15b4f280ee3c.sketch_text.stroke-134"),sQuery(id+"F0.wireOp",EDGE,"46c11c21-c6ca-42b8-9659-15b4f280ee3c.sketch_text.stroke-135"),sQuery(id+"F0.wireOp",EDGE,"46c11c21-c6ca-42b8-9659-15b4f280ee3c.sketch_text.stroke-136"),sQuery(id+"F0.wireOp",EDGE,"46c11c21-c6ca-42b8-9659-15b4f280ee3c.sketch_text.stroke-137"),sQuery(id+"F0.wireOp",EDGE,"46c11c21-c6ca-42b8-9659-15b4f280ee3c.sketch_text.stroke-138"),sQuery(id+"F0.wireOp",EDGE,"46c11c21-c6ca-42b8-9659-15b4f280ee3c.sketch_text.stroke-139"),sQuery(id+"F0.wireOp",EDGE,"46c11c21-c6ca-42b8-9659-15b4f280ee3c.sketch_text.stroke-140"),sQuery(id+"F0.wireOp",EDGE,"46c11c21-c6ca-42b8-9659-15b4f280ee3c.sketch_text.stroke-141"),sQuery(id+"F0.wireOp",EDGE,"46c11c21-c6ca-42b8-9659-15b4f280ee3c.sketch_text.stroke-142"),sQuery(id+"F0.wireOp",EDGE,"46c11c21-c6ca-42b8-9659-15b4f280ee3c.sketch_text.stroke-143"),sQuery(id+"F0.wireOp",EDGE,"46c11c21-c6ca-42b8-9659-15b4f280ee3c.sketch_text.stroke-144"),sQuery(id+"F0.wireOp",EDGE,"46c11c21-c6ca-42b8-9659-15b4f280ee3c.sketch_text.stroke-145"),sQuery(id+"F0.wireOp",EDGE,"46c11c21-c6ca-42b8-9659-15b4f280ee3c.sketch_text.stroke-146"),sQuery(id+"F0.wireOp",EDGE,"46c11c21-c6ca-42b8-9659-15b4f280ee3c.sketch_text.stroke-147"),sQuery(id+"F0.wireOp",EDGE,"46c11c21-c6ca-42b8-9659-15b4f280ee3c.sketch_text.stroke-148")])]});
            var Q2;
            Q2=makeQuery(id+"F1.opExtrude","SWEPT_BODY",BODY,{"disambiguationData":[OSD([sQuery(id+"F0.wireOp",EDGE,"46c11c21-c6ca-42b8-9659-15b4f280ee3c.sketch_text.stroke-101"),sQuery(id+"F0.wireOp",EDGE,"46c11c21-c6ca-42b8-9659-15b4f280ee3c.sketch_text.stroke-102"),sQuery(id+"F0.wireOp",EDGE,"46c11c21-c6ca-42b8-9659-15b4f280ee3c.sketch_text.stroke-103"),sQuery(id+"F0.wireOp",EDGE,"46c11c21-c6ca-42b8-9659-15b4f280ee3c.sketch_text.stroke-104"),sQuery(id+"F0.wireOp",EDGE,"46c11c21-c6ca-42b8-9659-15b4f280ee3c.sketch_text.stroke-105"),sQuery(id+"F0.wireOp",EDGE,"46c11c21-c6ca-42b8-9659-15b4f280ee3c.sketch_text.stroke-106"),sQuery(id+"F0.wireOp",EDGE,"46c11c21-c6ca-42b8-9659-15b4f280ee3c.sketch_text.stroke-107"),sQuery(id+"F0.wireOp",EDGE,"46c11c21-c6ca-42b8-9659-15b4f280ee3c.sketch_text.stroke-108"),sQuery(id+"F0.wireOp",EDGE,"46c11c21-c6ca-42b8-9659-15b4f280ee3c.sketch_text.stroke-109"),sQuery(id+"F0.wireOp",EDGE,"46c11c21-c6ca-42b8-9659-15b4f280ee3c.sketch_text.stroke-110"),sQuery(id+"F0.wireOp",EDGE,"46c11c21-c6ca-42b8-9659-15b4f280ee3c.sketch_text.stroke-111"),sQuery(id+"F0.wireOp",EDGE,"46c11c21-c6ca-42b8-9659-15b4f280ee3c.sketch_text.stroke-112"),sQuery(id+"F0.wireOp",EDGE,"46c11c21-c6ca-42b8-9659-15b4f280ee3c.sketch_text.stroke-113"),sQuery(id+"F0.wireOp",EDGE,"46c11c21-c6ca-42b8-9659-15b4f280ee3c.sketch_text.stroke-114")])]});
            var Q3;
            Q3=makeQuery(id+"F1.opExtrude","SWEPT_BODY",BODY,{"disambiguationData":[OSD([sQuery(id+"F0.wireOp",EDGE,"46c11c21-c6ca-42b8-9659-15b4f280ee3c.sketch_text.stroke-79"),sQuery(id+"F0.wireOp",EDGE,"46c11c21-c6ca-42b8-9659-15b4f280ee3c.sketch_text.stroke-80"),sQuery(id+"F0.wireOp",EDGE,"46c11c21-c6ca-42b8-9659-15b4f280ee3c.sketch_text.stroke-81"),sQuery(id+"F0.wireOp",EDGE,"46c11c21-c6ca-42b8-9659-15b4f280ee3c.sketch_text.stroke-82"),sQuery(id+"F0.wireOp",EDGE,"46c11c21-c6ca-42b8-9659-15b4f280ee3c.sketch_text.stroke-83"),sQuery(id+"F0.wireOp",EDGE,"46c11c21-c6ca-42b8-9659-15b4f280ee3c.sketch_text.stroke-84"),sQuery(id+"F0.wireOp",EDGE,"46c11c21-c6ca-42b8-9659-15b4f280ee3c.sketch_text.stroke-85"),sQuery(id+"F0.wireOp",EDGE,"46c11c21-c6ca-42b8-9659-15b4f280ee3c.sketch_text.stroke-86"),sQuery(id+"F0.wireOp",EDGE,"46c11c21-c6ca-42b8-9659-15b4f280ee3c.sketch_text.stroke-87"),sQuery(id+"F0.wireOp",EDGE,"46c11c21-c6ca-42b8-9659-15b4f280ee3c.sketch_text.stroke-88"),sQuery(id+"F0.wireOp",EDGE,"46c11c21-c6ca-42b8-9659-15b4f280ee3c.sketch_text.stroke-89"),sQuery(id+"F0.wireOp",EDGE,"46c11c21-c6ca-42b8-9659-15b4f280ee3c.sketch_text.stroke-90"),sQuery(id+"F0.wireOp",EDGE,"46c11c21-c6ca-42b8-9659-15b4f280ee3c.sketch_text.stroke-91"),sQuery(id+"F0.wireOp",EDGE,"46c11c21-c6ca-42b8-9659-15b4f280ee3c.sketch_text.stroke-92")])]});
            var Q4;
            Q4=makeQuery(id+"F1.opExtrude","SWEPT_BODY",BODY,{"disambiguationData":[OSD([sQuery(id+"F0.wireOp",EDGE,"E0.bottom"),sQuery(id+"F0.wireOp",EDGE,"E0.top"),sQuery(id+"F0.wireOp",EDGE,"E0.left"),sQuery(id+"F0.wireOp",EDGE,"E0.right"),sQuery(id+"F0.wireOp",EDGE,"E17.filletArc"),sQuery(id+"F0.wireOp",EDGE,"E18.filletArc"),sQuery(id+"F0.wireOp",EDGE,"E19.filletArc"),sQuery(id+"F0.wireOp",EDGE,"E20.filletArc")])]});
            var Q5;
            Q5=makeQuery(id+"F1.opExtrude","SWEPT_BODY",BODY,{"disambiguationData":[OSD([sQuery(id+"F0.wireOp",EDGE,"46c11c21-c6ca-42b8-9659-15b4f280ee3c.sketch_text.stroke-242"),sQuery(id+"F0.wireOp",EDGE,"46c11c21-c6ca-42b8-9659-15b4f280ee3c.sketch_text.stroke-243"),sQuery(id+"F0.wireOp",EDGE,"46c11c21-c6ca-42b8-9659-15b4f280ee3c.sketch_text.stroke-244"),sQuery(id+"F0.wireOp",EDGE,"46c11c21-c6ca-42b8-9659-15b4f280ee3c.sketch_text.stroke-245"),sQuery(id+"F0.wireOp",EDGE,"46c11c21-c6ca-42b8-9659-15b4f280ee3c.sketch_text.stroke-246"),sQuery(id+"F0.wireOp",EDGE,"46c11c21-c6ca-42b8-9659-15b4f280ee3c.sketch_text.stroke-247"),sQuery(id+"F0.wireOp",EDGE,"46c11c21-c6ca-42b8-9659-15b4f280ee3c.sketch_text.stroke-248"),sQuery(id+"F0.wireOp",EDGE,"46c11c21-c6ca-42b8-9659-15b4f280ee3c.sketch_text.stroke-249"),sQuery(id+"F0.wireOp",EDGE,"46c11c21-c6ca-42b8-9659-15b4f280ee3c.sketch_text.stroke-250"),sQuery(id+"F0.wireOp",EDGE,"46c11c21-c6ca-42b8-9659-15b4f280ee3c.sketch_text.stroke-251"),sQuery(id+"F0.wireOp",EDGE,"46c11c21-c6ca-42b8-9659-15b4f280ee3c.sketch_text.stroke-252"),sQuery(id+"F0.wireOp",EDGE,"46c11c21-c6ca-42b8-9659-15b4f280ee3c.sketch_text.stroke-253"),sQuery(id+"F0.wireOp",EDGE,"46c11c21-c6ca-42b8-9659-15b4f280ee3c.sketch_text.stroke-254"),sQuery(id+"F0.wireOp",EDGE,"46c11c21-c6ca-42b8-9659-15b4f280ee3c.sketch_text.stroke-255"),sQuery(id+"F0.wireOp",EDGE,"46c11c21-c6ca-42b8-9659-15b4f280ee3c.sketch_text.stroke-256"),sQuery(id+"F0.wireOp",EDGE,"46c11c21-c6ca-42b8-9659-15b4f280ee3c.sketch_text.stroke-257"),sQuery(id+"F0.wireOp",EDGE,"46c11c21-c6ca-42b8-9659-15b4f280ee3c.sketch_text.stroke-258"),sQuery(id+"F0.wireOp",EDGE,"46c11c21-c6ca-42b8-9659-15b4f280ee3c.sketch_text.stroke-259"),sQuery(id+"F0.wireOp",EDGE,"46c11c21-c6ca-42b8-9659-15b4f280ee3c.sketch_text.stroke-260")])]});
            var Q6;
            Q6=makeQuery(id+"F1.opExtrude","SWEPT_BODY",BODY,{"disambiguationData":[OSD([sQuery(id+"F0.wireOp",EDGE,"46c11c21-c6ca-42b8-9659-15b4f280ee3c.sketch_text.stroke-230"),sQuery(id+"F0.wireOp",EDGE,"46c11c21-c6ca-42b8-9659-15b4f280ee3c.sketch_text.stroke-231"),sQuery(id+"F0.wireOp",EDGE,"46c11c21-c6ca-42b8-9659-15b4f280ee3c.sketch_text.stroke-232"),sQuery(id+"F0.wireOp",EDGE,"46c11c21-c6ca-42b8-9659-15b4f280ee3c.sketch_text.stroke-233"),sQuery(id+"F0.wireOp",EDGE,"46c11c21-c6ca-42b8-9659-15b4f280ee3c.sketch_text.stroke-234"),sQuery(id+"F0.wireOp",EDGE,"46c11c21-c6ca-42b8-9659-15b4f280ee3c.sketch_text.stroke-235"),sQuery(id+"F0.wireOp",EDGE,"46c11c21-c6ca-42b8-9659-15b4f280ee3c.sketch_text.stroke-236"),sQuery(id+"F0.wireOp",EDGE,"46c11c21-c6ca-42b8-9659-15b4f280ee3c.sketch_text.stroke-237"),sQuery(id+"F0.wireOp",EDGE,"46c11c21-c6ca-42b8-9659-15b4f280ee3c.sketch_text.stroke-238"),sQuery(id+"F0.wireOp",EDGE,"46c11c21-c6ca-42b8-9659-15b4f280ee3c.sketch_text.stroke-239"),sQuery(id+"F0.wireOp",EDGE,"46c11c21-c6ca-42b8-9659-15b4f280ee3c.sketch_text.stroke-240"),sQuery(id+"F0.wireOp",EDGE,"46c11c21-c6ca-42b8-9659-15b4f280ee3c.sketch_text.stroke-241")])]});
            var Q7;
            Q7=makeQuery(id+"F1.opExtrude","SWEPT_BODY",BODY,{"disambiguationData":[OSD([sQuery(id+"F0.wireOp",EDGE,"46c11c21-c6ca-42b8-9659-15b4f280ee3c.sketch_text.stroke-218"),sQuery(id+"F0.wireOp",EDGE,"46c11c21-c6ca-42b8-9659-15b4f280ee3c.sketch_text.stroke-219"),sQuery(id+"F0.wireOp",EDGE,"46c11c21-c6ca-42b8-9659-15b4f280ee3c.sketch_text.stroke-220"),sQuery(id+"F0.wireOp",EDGE,"46c11c21-c6ca-42b8-9659-15b4f280ee3c.sketch_text.stroke-221"),sQuery(id+"F0.wireOp",EDGE,"46c11c21-c6ca-42b8-9659-15b4f280ee3c.sketch_text.stroke-222"),sQuery(id+"F0.wireOp",EDGE,"46c11c21-c6ca-42b8-9659-15b4f280ee3c.sketch_text.stroke-223")])]});
            var Q8;
            Q8=makeQuery(id+"F1.opExtrude","SWEPT_BODY",BODY,{"disambiguationData":[OSD([sQuery(id+"F0.wireOp",EDGE,"46c11c21-c6ca-42b8-9659-15b4f280ee3c.sketch_text.stroke-204"),sQuery(id+"F0.wireOp",EDGE,"46c11c21-c6ca-42b8-9659-15b4f280ee3c.sketch_text.stroke-205"),sQuery(id+"F0.wireOp",EDGE,"46c11c21-c6ca-42b8-9659-15b4f280ee3c.sketch_text.stroke-206"),sQuery(id+"F0.wireOp",EDGE,"46c11c21-c6ca-42b8-9659-15b4f280ee3c.sketch_text.stroke-207"),sQuery(id+"F0.wireOp",EDGE,"46c11c21-c6ca-42b8-9659-15b4f280ee3c.sketch_text.stroke-208"),sQuery(id+"F0.wireOp",EDGE,"46c11c21-c6ca-42b8-9659-15b4f280ee3c.sketch_text.stroke-209"),sQuery(id+"F0.wireOp",EDGE,"46c11c21-c6ca-42b8-9659-15b4f280ee3c.sketch_text.stroke-210"),sQuery(id+"F0.wireOp",EDGE,"46c11c21-c6ca-42b8-9659-15b4f280ee3c.sketch_text.stroke-211"),sQuery(id+"F0.wireOp",EDGE,"46c11c21-c6ca-42b8-9659-15b4f280ee3c.sketch_text.stroke-212"),sQuery(id+"F0.wireOp",EDGE,"46c11c21-c6ca-42b8-9659-15b4f280ee3c.sketch_text.stroke-213"),sQuery(id+"F0.wireOp",EDGE,"46c11c21-c6ca-42b8-9659-15b4f280ee3c.sketch_text.stroke-214"),sQuery(id+"F0.wireOp",EDGE,"46c11c21-c6ca-42b8-9659-15b4f280ee3c.sketch_text.stroke-215"),sQuery(id+"F0.wireOp",EDGE,"46c11c21-c6ca-42b8-9659-15b4f280ee3c.sketch_text.stroke-216"),sQuery(id+"F0.wireOp",EDGE,"46c11c21-c6ca-42b8-9659-15b4f280ee3c.sketch_text.stroke-217")])]});
            var Q9;
            Q9=makeQuery(id+"F1.opExtrude","SWEPT_BODY",BODY,{"disambiguationData":[OSD([sQuery(id+"F0.wireOp",EDGE,"46c11c21-c6ca-42b8-9659-15b4f280ee3c.sketch_text.stroke-29"),sQuery(id+"F0.wireOp",EDGE,"46c11c21-c6ca-42b8-9659-15b4f280ee3c.sketch_text.stroke-30"),sQuery(id+"F0.wireOp",EDGE,"46c11c21-c6ca-42b8-9659-15b4f280ee3c.sketch_text.stroke-31"),sQuery(id+"F0.wireOp",EDGE,"46c11c21-c6ca-42b8-9659-15b4f280ee3c.sketch_text.stroke-32"),sQuery(id+"F0.wireOp",EDGE,"46c11c21-c6ca-42b8-9659-15b4f280ee3c.sketch_text.stroke-33"),sQuery(id+"F0.wireOp",EDGE,"46c11c21-c6ca-42b8-9659-15b4f280ee3c.sketch_text.stroke-34"),sQuery(id+"F0.wireOp",EDGE,"46c11c21-c6ca-42b8-9659-15b4f280ee3c.sketch_text.stroke-35"),sQuery(id+"F0.wireOp",EDGE,"46c11c21-c6ca-42b8-9659-15b4f280ee3c.sketch_text.stroke-36"),sQuery(id+"F0.wireOp",EDGE,"46c11c21-c6ca-42b8-9659-15b4f280ee3c.sketch_text.stroke-37"),sQuery(id+"F0.wireOp",EDGE,"46c11c21-c6ca-42b8-9659-15b4f280ee3c.sketch_text.stroke-38"),sQuery(id+"F0.wireOp",EDGE,"46c11c21-c6ca-42b8-9659-15b4f280ee3c.sketch_text.stroke-39"),sQuery(id+"F0.wireOp",EDGE,"46c11c21-c6ca-42b8-9659-15b4f280ee3c.sketch_text.stroke-40"),sQuery(id+"F0.wireOp",EDGE,"46c11c21-c6ca-42b8-9659-15b4f280ee3c.sketch_text.stroke-41"),sQuery(id+"F0.wireOp",EDGE,"46c11c21-c6ca-42b8-9659-15b4f280ee3c.sketch_text.stroke-42"),sQuery(id+"F0.wireOp",EDGE,"46c11c21-c6ca-42b8-9659-15b4f280ee3c.sketch_text.stroke-43"),sQuery(id+"F0.wireOp",EDGE,"46c11c21-c6ca-42b8-9659-15b4f280ee3c.sketch_text.stroke-44"),sQuery(id+"F0.wireOp",EDGE,"46c11c21-c6ca-42b8-9659-15b4f280ee3c.sketch_text.stroke-45"),sQuery(id+"F0.wireOp",EDGE,"46c11c21-c6ca-42b8-9659-15b4f280ee3c.sketch_text.stroke-46"),sQuery(id+"F0.wireOp",EDGE,"46c11c21-c6ca-42b8-9659-15b4f280ee3c.sketch_text.stroke-47")])]});
            var Q10;
            Q10=makeQuery(id+"F1.opExtrude","SWEPT_BODY",BODY,{"disambiguationData":[OSD([sQuery(id+"F0.wireOp",EDGE,"46c11c21-c6ca-42b8-9659-15b4f280ee3c.sketch_text.stroke-15"),sQuery(id+"F0.wireOp",EDGE,"46c11c21-c6ca-42b8-9659-15b4f280ee3c.sketch_text.stroke-16"),sQuery(id+"F0.wireOp",EDGE,"46c11c21-c6ca-42b8-9659-15b4f280ee3c.sketch_text.stroke-17"),sQuery(id+"F0.wireOp",EDGE,"46c11c21-c6ca-42b8-9659-15b4f280ee3c.sketch_text.stroke-18"),sQuery(id+"F0.wireOp",EDGE,"46c11c21-c6ca-42b8-9659-15b4f280ee3c.sketch_text.stroke-19"),sQuery(id+"F0.wireOp",EDGE,"46c11c21-c6ca-42b8-9659-15b4f280ee3c.sketch_text.stroke-20"),sQuery(id+"F0.wireOp",EDGE,"46c11c21-c6ca-42b8-9659-15b4f280ee3c.sketch_text.stroke-21"),sQuery(id+"F0.wireOp",EDGE,"46c11c21-c6ca-42b8-9659-15b4f280ee3c.sketch_text.stroke-22"),sQuery(id+"F0.wireOp",EDGE,"46c11c21-c6ca-42b8-9659-15b4f280ee3c.sketch_text.stroke-23"),sQuery(id+"F0.wireOp",EDGE,"46c11c21-c6ca-42b8-9659-15b4f280ee3c.sketch_text.stroke-24"),sQuery(id+"F0.wireOp",EDGE,"46c11c21-c6ca-42b8-9659-15b4f280ee3c.sketch_text.stroke-25"),sQuery(id+"F0.wireOp",EDGE,"46c11c21-c6ca-42b8-9659-15b4f280ee3c.sketch_text.stroke-26"),sQuery(id+"F0.wireOp",EDGE,"46c11c21-c6ca-42b8-9659-15b4f280ee3c.sketch_text.stroke-27"),sQuery(id+"F0.wireOp",EDGE,"46c11c21-c6ca-42b8-9659-15b4f280ee3c.sketch_text.stroke-28")])]});
            var Q11;
            Q11=makeQuery(id+"F1.opExtrude","SWEPT_BODY",BODY,{"disambiguationData":[OSD([sQuery(id+"F0.wireOp",EDGE,"E3"),sQuery(id+"F0.wireOp",EDGE,"E4"),sQuery(id+"F0.wireOp",EDGE,"E5"),sQuery(id+"F0.wireOp",EDGE,"E6.0"),sQuery(id+"F0.wireOp",EDGE,"E6.1"),sQuery(id+"F0.wireOp",EDGE,"E6.2"),sQuery(id+"F0.wireOp",EDGE,"E9.filletArc"),sQuery(id+"F0.wireOp",EDGE,"E10.filletArc"),sQuery(id+"F0.wireOp",EDGE,"E12.6.MirrorCS"),sQuery(id+"F0.wireOp",EDGE,"E12.7.MirrorCS"),sQuery(id+"F0.wireOp",EDGE,"E12.8.MirrorCS"),sQuery(id+"F0.wireOp",EDGE,"E12.10.MirrorCS"),sQuery(id+"F0.wireOp",EDGE,"E12.12.MirrorCS"),sQuery(id+"F0.wireOp",EDGE,"E12.13.MirrorCS"),sQuery(id+"F0.wireOp",EDGE,"E12.14.MirrorCS"),sQuery(id+"F0.wireOp",EDGE,"E12.15.MirrorCS"),sQuery(id+"F0.wireOp",EDGE,"E29.filletArc"),sQuery(id+"F0.wireOp",EDGE,"E30.filletArc"),sQuery(id+"F0.wireOp",EDGE,"E31.filletArc"),sQuery(id+"F0.wireOp",EDGE,"E32.filletArc"),sQuery(id+"F0.wireOp",EDGE,"E33.filletArc"),sQuery(id+"F0.wireOp",EDGE,"E34.filletArc"),sQuery(id+"F0.wireOp",EDGE,"E35.filletArc"),sQuery(id+"F0.wireOp",EDGE,"E36.filletArc"),sQuery(id+"F0.wireOp",EDGE,"E37.filletArc"),sQuery(id+"F0.wireOp",EDGE,"E38.filletArc")])]});
            var Q12;
            Q12=makeQuery(id+"F1.opExtrude","SWEPT_BODY",BODY,{"disambiguationData":[OSD([sQuery(id+"F0.wireOp",EDGE,"E12.1.MirrorCS"),sQuery(id+"F0.wireOp",EDGE,"E12.3.MirrorCS"),sQuery(id+"F0.wireOp",EDGE,"E12.4.MirrorCS"),sQuery(id+"F0.wireOp",EDGE,"E12.5.MirrorCS"),sQuery(id+"F0.wireOp",EDGE,"E21.filletArc"),sQuery(id+"F0.wireOp",EDGE,"E22.filletArc"),sQuery(id+"F0.wireOp",EDGE,"E23.filletArc"),sQuery(id+"F0.wireOp",EDGE,"E24.filletArc")])]});
            var Q13;
            Q13=makeQuery(id+"F1.opExtrude","SWEPT_BODY",BODY,{"disambiguationData":[OSD([sQuery(id+"F0.wireOp",EDGE,"E41"),sQuery(id+"F0.wireOp",EDGE,"E42"),sQuery(id+"F0.wireOp",EDGE,"E43"),sQuery(id+"F0.wireOp",EDGE,"E54.trimOffspring")])]});
            var Q14;
            Q14=makeQuery(id+"F1.opExtrude","SWEPT_BODY",BODY,{"disambiguationData":[OSD([sQuery(id+"F0.wireOp",EDGE,"46c11c21-c6ca-42b8-9659-15b4f280ee3c.sketch_text.stroke-163"),sQuery(id+"F0.wireOp",EDGE,"46c11c21-c6ca-42b8-9659-15b4f280ee3c.sketch_text.stroke-164"),sQuery(id+"F0.wireOp",EDGE,"46c11c21-c6ca-42b8-9659-15b4f280ee3c.sketch_text.stroke-165"),sQuery(id+"F0.wireOp",EDGE,"46c11c21-c6ca-42b8-9659-15b4f280ee3c.sketch_text.stroke-166"),sQuery(id+"F0.wireOp",EDGE,"46c11c21-c6ca-42b8-9659-15b4f280ee3c.sketch_text.stroke-167"),sQuery(id+"F0.wireOp",EDGE,"46c11c21-c6ca-42b8-9659-15b4f280ee3c.sketch_text.stroke-168"),sQuery(id+"F0.wireOp",EDGE,"46c11c21-c6ca-42b8-9659-15b4f280ee3c.sketch_text.stroke-169"),sQuery(id+"F0.wireOp",EDGE,"46c11c21-c6ca-42b8-9659-15b4f280ee3c.sketch_text.stroke-170"),sQuery(id+"F0.wireOp",EDGE,"46c11c21-c6ca-42b8-9659-15b4f280ee3c.sketch_text.stroke-171"),sQuery(id+"F0.wireOp",EDGE,"46c11c21-c6ca-42b8-9659-15b4f280ee3c.sketch_text.stroke-172"),sQuery(id+"F0.wireOp",EDGE,"46c11c21-c6ca-42b8-9659-15b4f280ee3c.sketch_text.stroke-173"),sQuery(id+"F0.wireOp",EDGE,"46c11c21-c6ca-42b8-9659-15b4f280ee3c.sketch_text.stroke-174"),sQuery(id+"F0.wireOp",EDGE,"46c11c21-c6ca-42b8-9659-15b4f280ee3c.sketch_text.stroke-175"),sQuery(id+"F0.wireOp",EDGE,"46c11c21-c6ca-42b8-9659-15b4f280ee3c.sketch_text.stroke-176")])]});
            var Q15;
            Q15=makeQuery(id+"F1.opExtrude","SWEPT_BODY",BODY,{"disambiguationData":[OSD([sQuery(id+"F0.wireOp",EDGE,"46c11c21-c6ca-42b8-9659-15b4f280ee3c.sketch_text.stroke-115"),sQuery(id+"F0.wireOp",EDGE,"46c11c21-c6ca-42b8-9659-15b4f280ee3c.sketch_text.stroke-116"),sQuery(id+"F0.wireOp",EDGE,"46c11c21-c6ca-42b8-9659-15b4f280ee3c.sketch_text.stroke-117"),sQuery(id+"F0.wireOp",EDGE,"46c11c21-c6ca-42b8-9659-15b4f280ee3c.sketch_text.stroke-118"),sQuery(id+"F0.wireOp",EDGE,"46c11c21-c6ca-42b8-9659-15b4f280ee3c.sketch_text.stroke-119"),sQuery(id+"F0.wireOp",EDGE,"46c11c21-c6ca-42b8-9659-15b4f280ee3c.sketch_text.stroke-120"),sQuery(id+"F0.wireOp",EDGE,"46c11c21-c6ca-42b8-9659-15b4f280ee3c.sketch_text.stroke-121"),sQuery(id+"F0.wireOp",EDGE,"46c11c21-c6ca-42b8-9659-15b4f280ee3c.sketch_text.stroke-122"),sQuery(id+"F0.wireOp",EDGE,"46c11c21-c6ca-42b8-9659-15b4f280ee3c.sketch_text.stroke-123"),sQuery(id+"F0.wireOp",EDGE,"46c11c21-c6ca-42b8-9659-15b4f280ee3c.sketch_text.stroke-124"),sQuery(id+"F0.wireOp",EDGE,"46c11c21-c6ca-42b8-9659-15b4f280ee3c.sketch_text.stroke-125"),sQuery(id+"F0.wireOp",EDGE,"46c11c21-c6ca-42b8-9659-15b4f280ee3c.sketch_text.stroke-126"),sQuery(id+"F0.wireOp",EDGE,"46c11c21-c6ca-42b8-9659-15b4f280ee3c.sketch_text.stroke-127"),sQuery(id+"F0.wireOp",EDGE,"46c11c21-c6ca-42b8-9659-15b4f280ee3c.sketch_text.stroke-128"),sQuery(id+"F0.wireOp",EDGE,"46c11c21-c6ca-42b8-9659-15b4f280ee3c.sketch_text.stroke-129"),sQuery(id+"F0.wireOp",EDGE,"46c11c21-c6ca-42b8-9659-15b4f280ee3c.sketch_text.stroke-130"),sQuery(id+"F0.wireOp",EDGE,"46c11c21-c6ca-42b8-9659-15b4f280ee3c.sketch_text.stroke-131"),sQuery(id+"F0.wireOp",EDGE,"46c11c21-c6ca-42b8-9659-15b4f280ee3c.sketch_text.stroke-132"),sQuery(id+"F0.wireOp",EDGE,"46c11c21-c6ca-42b8-9659-15b4f280ee3c.sketch_text.stroke-133")])]});
            var Q16;
            Q16=makeQuery(id+"F1.opExtrude","SWEPT_BODY",BODY,{"disambiguationData":[OSD([sQuery(id+"F0.wireOp",EDGE,"46c11c21-c6ca-42b8-9659-15b4f280ee3c.sketch_text.stroke-185"),sQuery(id+"F0.wireOp",EDGE,"46c11c21-c6ca-42b8-9659-15b4f280ee3c.sketch_text.stroke-186"),sQuery(id+"F0.wireOp",EDGE,"46c11c21-c6ca-42b8-9659-15b4f280ee3c.sketch_text.stroke-187"),sQuery(id+"F0.wireOp",EDGE,"46c11c21-c6ca-42b8-9659-15b4f280ee3c.sketch_text.stroke-188"),sQuery(id+"F0.wireOp",EDGE,"46c11c21-c6ca-42b8-9659-15b4f280ee3c.sketch_text.stroke-189"),sQuery(id+"F0.wireOp",EDGE,"46c11c21-c6ca-42b8-9659-15b4f280ee3c.sketch_text.stroke-190"),sQuery(id+"F0.wireOp",EDGE,"46c11c21-c6ca-42b8-9659-15b4f280ee3c.sketch_text.stroke-191"),sQuery(id+"F0.wireOp",EDGE,"46c11c21-c6ca-42b8-9659-15b4f280ee3c.sketch_text.stroke-192"),sQuery(id+"F0.wireOp",EDGE,"46c11c21-c6ca-42b8-9659-15b4f280ee3c.sketch_text.stroke-193"),sQuery(id+"F0.wireOp",EDGE,"46c11c21-c6ca-42b8-9659-15b4f280ee3c.sketch_text.stroke-194"),sQuery(id+"F0.wireOp",EDGE,"46c11c21-c6ca-42b8-9659-15b4f280ee3c.sketch_text.stroke-195"),sQuery(id+"F0.wireOp",EDGE,"46c11c21-c6ca-42b8-9659-15b4f280ee3c.sketch_text.stroke-196"),sQuery(id+"F0.wireOp",EDGE,"46c11c21-c6ca-42b8-9659-15b4f280ee3c.sketch_text.stroke-197"),sQuery(id+"F0.wireOp",EDGE,"46c11c21-c6ca-42b8-9659-15b4f280ee3c.sketch_text.stroke-198"),sQuery(id+"F0.wireOp",EDGE,"46c11c21-c6ca-42b8-9659-15b4f280ee3c.sketch_text.stroke-199"),sQuery(id+"F0.wireOp",EDGE,"46c11c21-c6ca-42b8-9659-15b4f280ee3c.sketch_text.stroke-200"),sQuery(id+"F0.wireOp",EDGE,"46c11c21-c6ca-42b8-9659-15b4f280ee3c.sketch_text.stroke-201"),sQuery(id+"F0.wireOp",EDGE,"46c11c21-c6ca-42b8-9659-15b4f280ee3c.sketch_text.stroke-202"),sQuery(id+"F0.wireOp",EDGE,"46c11c21-c6ca-42b8-9659-15b4f280ee3c.sketch_text.stroke-203")])]});
            var Q17;
            Q17=makeQuery(id+"F1.opExtrude","SWEPT_BODY",BODY,{"disambiguationData":[OSD([sQuery(id+"F0.wireOp",EDGE,"E46.trimOffspring"),sQuery(id+"F0.wireOp",EDGE,"E48.trimOffspring"),sQuery(id+"F0.wireOp",EDGE,"E51.trimOffspring"),sQuery(id+"F0.wireOp",EDGE,"E53.trimOffspring")])]});
            var Q18;
            Q18=makeQuery(id+"F1.opExtrude","SWEPT_BODY",BODY,{"disambiguationData":[OSD([sQuery(id+"F0.wireOp",EDGE,"E11.right"),sQuery(id+"F0.wireOp",EDGE,"E11.left"),sQuery(id+"F0.wireOp",EDGE,"E11.top"),sQuery(id+"F0.wireOp",EDGE,"E11.bottom"),sQuery(id+"F0.wireOp",EDGE,"E25.filletArc"),sQuery(id+"F0.wireOp",EDGE,"E26.filletArc"),sQuery(id+"F0.wireOp",EDGE,"E27.filletArc"),sQuery(id+"F0.wireOp",EDGE,"E28.filletArc")])]});
            var Q19;
            Q19=makeQuery(id+"F1.opExtrude","SWEPT_BODY",BODY,{"disambiguationData":[OSD([sQuery(id+"F0.wireOp",EDGE,"46c11c21-c6ca-42b8-9659-15b4f280ee3c.sketch_text.stroke-224"),sQuery(id+"F0.wireOp",EDGE,"46c11c21-c6ca-42b8-9659-15b4f280ee3c.sketch_text.stroke-225"),sQuery(id+"F0.wireOp",EDGE,"46c11c21-c6ca-42b8-9659-15b4f280ee3c.sketch_text.stroke-226"),sQuery(id+"F0.wireOp",EDGE,"46c11c21-c6ca-42b8-9659-15b4f280ee3c.sketch_text.stroke-227"),sQuery(id+"F0.wireOp",EDGE,"46c11c21-c6ca-42b8-9659-15b4f280ee3c.sketch_text.stroke-228"),sQuery(id+"F0.wireOp",EDGE,"46c11c21-c6ca-42b8-9659-15b4f280ee3c.sketch_text.stroke-229")])]});
            var Q20;
            Q20=makeQuery(id+"F1.opExtrude","SWEPT_BODY",BODY,{"disambiguationData":[OSD([sQuery(id+"F0.wireOp",EDGE,"46c11c21-c6ca-42b8-9659-15b4f280ee3c.sketch_text.stroke-60"),sQuery(id+"F0.wireOp",EDGE,"46c11c21-c6ca-42b8-9659-15b4f280ee3c.sketch_text.stroke-61"),sQuery(id+"F0.wireOp",EDGE,"46c11c21-c6ca-42b8-9659-15b4f280ee3c.sketch_text.stroke-62"),sQuery(id+"F0.wireOp",EDGE,"46c11c21-c6ca-42b8-9659-15b4f280ee3c.sketch_text.stroke-63"),sQuery(id+"F0.wireOp",EDGE,"46c11c21-c6ca-42b8-9659-15b4f280ee3c.sketch_text.stroke-64"),sQuery(id+"F0.wireOp",EDGE,"46c11c21-c6ca-42b8-9659-15b4f280ee3c.sketch_text.stroke-65"),sQuery(id+"F0.wireOp",EDGE,"46c11c21-c6ca-42b8-9659-15b4f280ee3c.sketch_text.stroke-66"),sQuery(id+"F0.wireOp",EDGE,"46c11c21-c6ca-42b8-9659-15b4f280ee3c.sketch_text.stroke-67"),sQuery(id+"F0.wireOp",EDGE,"46c11c21-c6ca-42b8-9659-15b4f280ee3c.sketch_text.stroke-68"),sQuery(id+"F0.wireOp",EDGE,"46c11c21-c6ca-42b8-9659-15b4f280ee3c.sketch_text.stroke-69"),sQuery(id+"F0.wireOp",EDGE,"46c11c21-c6ca-42b8-9659-15b4f280ee3c.sketch_text.stroke-70"),sQuery(id+"F0.wireOp",EDGE,"46c11c21-c6ca-42b8-9659-15b4f280ee3c.sketch_text.stroke-71"),sQuery(id+"F0.wireOp",EDGE,"46c11c21-c6ca-42b8-9659-15b4f280ee3c.sketch_text.stroke-72"),sQuery(id+"F0.wireOp",EDGE,"46c11c21-c6ca-42b8-9659-15b4f280ee3c.sketch_text.stroke-73"),sQuery(id+"F0.wireOp",EDGE,"46c11c21-c6ca-42b8-9659-15b4f280ee3c.sketch_text.stroke-74"),sQuery(id+"F0.wireOp",EDGE,"46c11c21-c6ca-42b8-9659-15b4f280ee3c.sketch_text.stroke-75"),sQuery(id+"F0.wireOp",EDGE,"46c11c21-c6ca-42b8-9659-15b4f280ee3c.sketch_text.stroke-76"),sQuery(id+"F0.wireOp",EDGE,"46c11c21-c6ca-42b8-9659-15b4f280ee3c.sketch_text.stroke-77"),sQuery(id+"F0.wireOp",EDGE,"46c11c21-c6ca-42b8-9659-15b4f280ee3c.sketch_text.stroke-78")])]});
            var Q21;
            Q21=makeQuery(id+"F1.opExtrude","SWEPT_BODY",BODY,{"disambiguationData":[OSD([sQuery(id+"F0.wireOp",EDGE,"E39"),sQuery(id+"F0.wireOp",EDGE,"E40"),sQuery(id+"F0.wireOp",EDGE,"E44.trimOffspring"),sQuery(id+"F0.wireOp",EDGE,"E52.trimOffspring")])]});
            var Q22;
            Q22=makeQuery(id+"F1.opExtrude","SWEPT_BODY",BODY,{"disambiguationData":[OSD([sQuery(id+"F0.wireOp",EDGE,"46c11c21-c6ca-42b8-9659-15b4f280ee3c.sketch_text.stroke-177"),sQuery(id+"F0.wireOp",EDGE,"46c11c21-c6ca-42b8-9659-15b4f280ee3c.sketch_text.stroke-178"),sQuery(id+"F0.wireOp",EDGE,"46c11c21-c6ca-42b8-9659-15b4f280ee3c.sketch_text.stroke-179"),sQuery(id+"F0.wireOp",EDGE,"46c11c21-c6ca-42b8-9659-15b4f280ee3c.sketch_text.stroke-180"),sQuery(id+"F0.wireOp",EDGE,"46c11c21-c6ca-42b8-9659-15b4f280ee3c.sketch_text.stroke-181"),sQuery(id+"F0.wireOp",EDGE,"46c11c21-c6ca-42b8-9659-15b4f280ee3c.sketch_text.stroke-182"),sQuery(id+"F0.wireOp",EDGE,"46c11c21-c6ca-42b8-9659-15b4f280ee3c.sketch_text.stroke-183"),sQuery(id+"F0.wireOp",EDGE,"46c11c21-c6ca-42b8-9659-15b4f280ee3c.sketch_text.stroke-184")])]});
            var Q23;
            Q23=makeQuery(id+"F1.opExtrude","SWEPT_BODY",BODY,{"disambiguationData":[OSD([sQuery(id+"F0.wireOp",EDGE,"46c11c21-c6ca-42b8-9659-15b4f280ee3c.sketch_text.stroke-0"),sQuery(id+"F0.wireOp",EDGE,"46c11c21-c6ca-42b8-9659-15b4f280ee3c.sketch_text.stroke-1"),sQuery(id+"F0.wireOp",EDGE,"46c11c21-c6ca-42b8-9659-15b4f280ee3c.sketch_text.stroke-2"),sQuery(id+"F0.wireOp",EDGE,"46c11c21-c6ca-42b8-9659-15b4f280ee3c.sketch_text.stroke-3"),sQuery(id+"F0.wireOp",EDGE,"46c11c21-c6ca-42b8-9659-15b4f280ee3c.sketch_text.stroke-4"),sQuery(id+"F0.wireOp",EDGE,"46c11c21-c6ca-42b8-9659-15b4f280ee3c.sketch_text.stroke-5"),sQuery(id+"F0.wireOp",EDGE,"46c11c21-c6ca-42b8-9659-15b4f280ee3c.sketch_text.stroke-6"),sQuery(id+"F0.wireOp",EDGE,"46c11c21-c6ca-42b8-9659-15b4f280ee3c.sketch_text.stroke-7"),sQuery(id+"F0.wireOp",EDGE,"46c11c21-c6ca-42b8-9659-15b4f280ee3c.sketch_text.stroke-8"),sQuery(id+"F0.wireOp",EDGE,"46c11c21-c6ca-42b8-9659-15b4f280ee3c.sketch_text.stroke-9"),sQuery(id+"F0.wireOp",EDGE,"46c11c21-c6ca-42b8-9659-15b4f280ee3c.sketch_text.stroke-10"),sQuery(id+"F0.wireOp",EDGE,"46c11c21-c6ca-42b8-9659-15b4f280ee3c.sketch_text.stroke-11"),sQuery(id+"F0.wireOp",EDGE,"46c11c21-c6ca-42b8-9659-15b4f280ee3c.sketch_text.stroke-12"),sQuery(id+"F0.wireOp",EDGE,"46c11c21-c6ca-42b8-9659-15b4f280ee3c.sketch_text.stroke-13"),sQuery(id+"F0.wireOp",EDGE,"46c11c21-c6ca-42b8-9659-15b4f280ee3c.sketch_text.stroke-14")])]});
            var Q24;
            Q24=makeQuery(id+"F1.opExtrude","SWEPT_BODY",BODY,{"disambiguationData":[OSD([sQuery(id+"F0.wireOp",EDGE,"46c11c21-c6ca-42b8-9659-15b4f280ee3c.sketch_text.stroke-48"),sQuery(id+"F0.wireOp",EDGE,"46c11c21-c6ca-42b8-9659-15b4f280ee3c.sketch_text.stroke-49"),sQuery(id+"F0.wireOp",EDGE,"46c11c21-c6ca-42b8-9659-15b4f280ee3c.sketch_text.stroke-50"),sQuery(id+"F0.wireOp",EDGE,"46c11c21-c6ca-42b8-9659-15b4f280ee3c.sketch_text.stroke-51"),sQuery(id+"F0.wireOp",EDGE,"46c11c21-c6ca-42b8-9659-15b4f280ee3c.sketch_text.stroke-52"),sQuery(id+"F0.wireOp",EDGE,"46c11c21-c6ca-42b8-9659-15b4f280ee3c.sketch_text.stroke-53"),sQuery(id+"F0.wireOp",EDGE,"46c11c21-c6ca-42b8-9659-15b4f280ee3c.sketch_text.stroke-54"),sQuery(id+"F0.wireOp",EDGE,"46c11c21-c6ca-42b8-9659-15b4f280ee3c.sketch_text.stroke-55"),sQuery(id+"F0.wireOp",EDGE,"46c11c21-c6ca-42b8-9659-15b4f280ee3c.sketch_text.stroke-56"),sQuery(id+"F0.wireOp",EDGE,"46c11c21-c6ca-42b8-9659-15b4f280ee3c.sketch_text.stroke-57"),sQuery(id+"F0.wireOp",EDGE,"46c11c21-c6ca-42b8-9659-15b4f280ee3c.sketch_text.stroke-58"),sQuery(id+"F0.wireOp",EDGE,"46c11c21-c6ca-42b8-9659-15b4f280ee3c.sketch_text.stroke-59")])]});
            var Q25;
            Q25=makeQuery(id+"F1.opExtrude","SWEPT_BODY",BODY,{"disambiguationData":[OSD([sQuery(id+"F0.wireOp",EDGE,"46c11c21-c6ca-42b8-9659-15b4f280ee3c.sketch_text.stroke-93"),sQuery(id+"F0.wireOp",EDGE,"46c11c21-c6ca-42b8-9659-15b4f280ee3c.sketch_text.stroke-94"),sQuery(id+"F0.wireOp",EDGE,"46c11c21-c6ca-42b8-9659-15b4f280ee3c.sketch_text.stroke-95"),sQuery(id+"F0.wireOp",EDGE,"46c11c21-c6ca-42b8-9659-15b4f280ee3c.sketch_text.stroke-96"),sQuery(id+"F0.wireOp",EDGE,"46c11c21-c6ca-42b8-9659-15b4f280ee3c.sketch_text.stroke-97"),sQuery(id+"F0.wireOp",EDGE,"46c11c21-c6ca-42b8-9659-15b4f280ee3c.sketch_text.stroke-98"),sQuery(id+"F0.wireOp",EDGE,"46c11c21-c6ca-42b8-9659-15b4f280ee3c.sketch_text.stroke-99"),sQuery(id+"F0.wireOp",EDGE,"46c11c21-c6ca-42b8-9659-15b4f280ee3c.sketch_text.stroke-100")])]});
            var Q26;
            Q26=makeQuery(id+"F1.opExtrude","SWEPT_BODY",BODY,{"disambiguationData":[OSD([sQuery(id+"F0.wireOp",EDGE,"E1.bottom"),sQuery(id+"F0.wireOp",EDGE,"E1.top"),sQuery(id+"F0.wireOp",EDGE,"E1.left"),sQuery(id+"F0.wireOp",EDGE,"E1.right"),sQuery(id+"F0.wireOp",EDGE,"E13.filletArc"),sQuery(id+"F0.wireOp",EDGE,"E14.filletArc"),sQuery(id+"F0.wireOp",EDGE,"E15.filletArc"),sQuery(id+"F0.wireOp",EDGE,"E16.filletArc")])]});
            var Q27;
            Q27=makeQuery(id+"F1.opExtrude","SWEPT_BODY",BODY,{"disambiguationData":[OSD([sQuery(id+"F0.wireOp",EDGE,"E45"),sQuery(id+"F0.wireOp",EDGE,"E47"),sQuery(id+"F0.wireOp",EDGE,"E49.trimOffspring"),sQuery(id+"F0.wireOp",EDGE,"E50.trimOffspring")])]});
            var Q28;
            Q28=qCreatedBy(makeId("Origin.pointOp"),VERTEX);
            transform(context, id + "F2", {"entities" : qUnion([Q0, Q1, Q2, Q3, Q4, Q5, Q6, Q7, Q8, Q9, Q10, Q11, Q12, Q13, Q14, Q15, Q16, Q17, Q18, Q19, Q20, Q21, Q22, Q23, Q24, Q25, Q26, Q27]), "transformType" : TransformType.SCALE_UNIFORMLY, "scale" : .357, "makeCopy" : false, "scalePoint" : qUnion([Q28])});
        }
        {
            var Q0;
            Q0=qCreatedBy(makeId("Top.planeOp"),FACE);
            var sketch = newSketch(context, id + "F3", { "sketchPlane" : qUnion([Q0])});
            skText(sketch, "E55", { "text": "C O R E   M O T O R\nC O N T R O L L E R", "fontName": "Arimo-Bold.ttf"});
            const initialGuessF3  = {"E55": [-0.0235, -0.0035, 1, 0, 0.0025]};
            skSetInitialGuess(sketch, initialGuessF3);
            skSolve(sketch);
        }
        {
            var Q0;
            Q0 = qSketchRegion(id + "F3", true);
            extrude(context, id + "F4", {"entities" : qUnion([Q0]), "depth" : .1 * mm});
        }
    });
